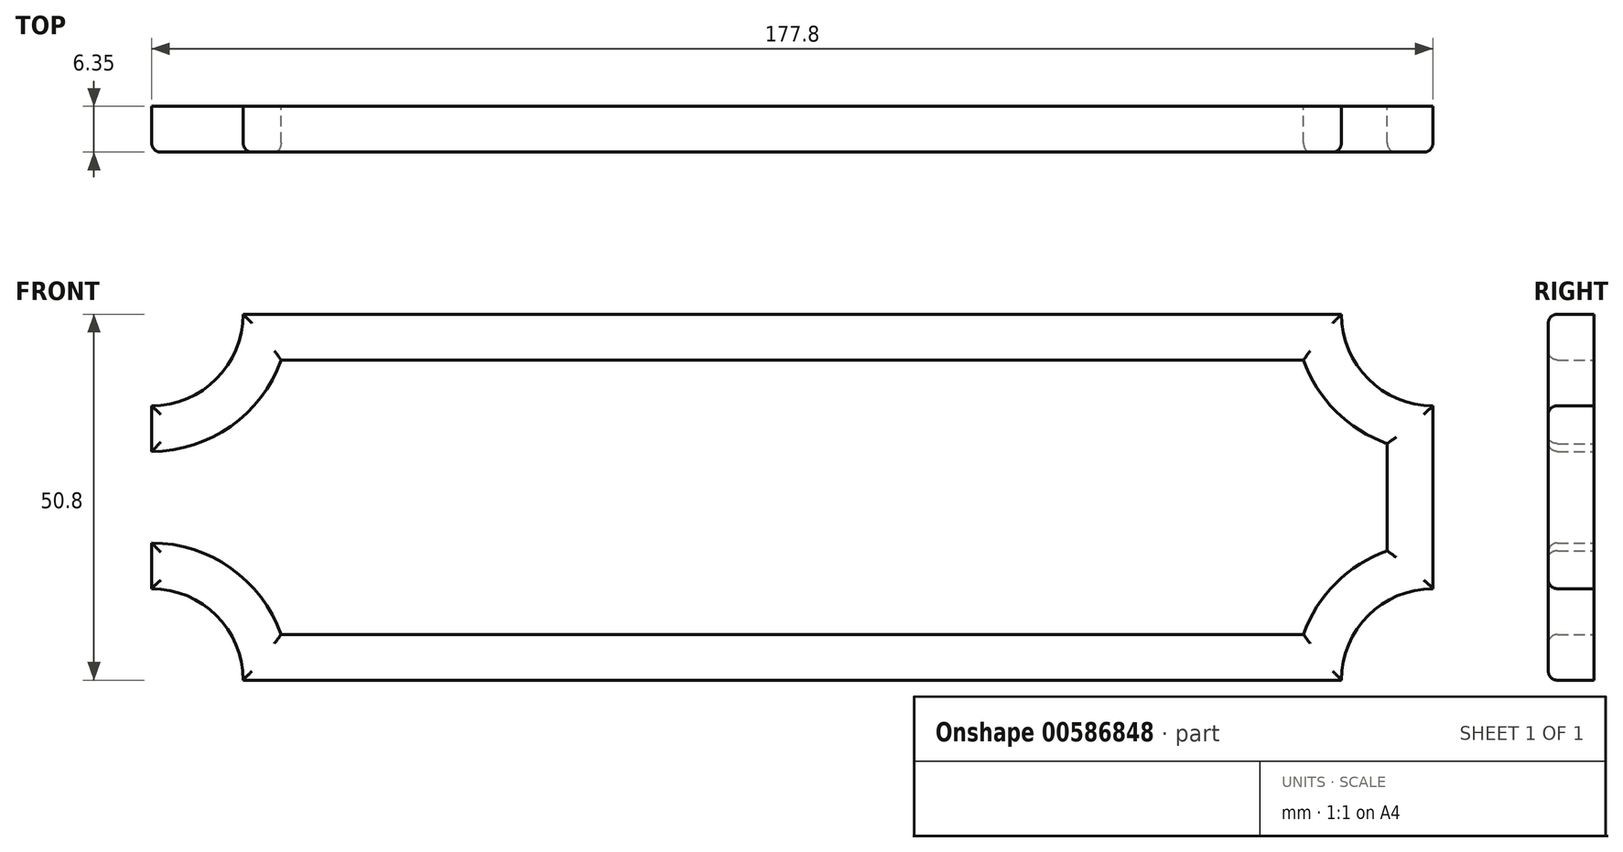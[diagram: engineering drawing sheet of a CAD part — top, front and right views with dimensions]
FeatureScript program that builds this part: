
annotation { "Feature Type Name" : "Feature", "Feature Type Description" : "" }
export const myFeature = defineFeature(function(context is Context, id is Id, definition is map)
    precondition{}
    {
        {
            var Q0;
            Q0=qCreatedBy(makeId("Front.planeOp"),FACE);
            var sketch = newSketch(context, id + "F0", { "sketchPlane" : qUnion([Q0])});
            skLineSegment(sketch, "E0.bottom", {"start": v(-76.2, -25.4) * mm, "end": v(76.2, -25.4) * mm});
            skLineSegment(sketch, "E0.top", {"start": v(-76.2, 25.4) * mm, "end": v(76.2, 25.4) * mm});
            skPoint(sketch, "E0.middle", {"position": v(0, 0) * mm});
            skLineSegment(sketch, "E1.left", {"start": v(-88.9, 12.7) * mm, "end": v(-88.9, -12.7) * mm});
            skLineSegment(sketch, "E1.right", {"start": v(88.9, 12.7) * mm, "end": v(88.9, -12.7) * mm});
            skArc(sketch, "E2", {"start": v(-76.2, -25.4) * mm, "mid": v(-79.92, -16.42) * mm, "end": v(-88.9, -12.7) * mm});
            skArc(sketch, "E3", {"start": v(-88.9, 12.7) * mm, "mid": v(-79.92, 16.42) * mm, "end": v(-76.2, 25.4) * mm});
            skArc(sketch, "E4", {"start": v(76.2, 25.4) * mm, "mid": v(79.92, 16.42) * mm, "end": v(88.9, 12.7) * mm});
            skArc(sketch, "E5", {"start": v(88.9, -12.7) * mm, "mid": v(79.92, -16.42) * mm, "end": v(76.2, -25.4) * mm});
            skArc(sketch, "E6.0", {"start": v(-88.9, 6.35) * mm, "mid": v(-75.43, 11.93) * mm, "end": v(-69.85, 25.4) * mm});
            skArc(sketch, "E7.0", {"start": v(-69.85, -25.4) * mm, "mid": v(-75.43, -11.93) * mm, "end": v(-88.9, -6.35) * mm});
            skArc(sketch, "E8.0", {"start": v(88.9, -6.35) * mm, "mid": v(75.43, -11.93) * mm, "end": v(69.85, -25.4) * mm});
            skArc(sketch, "E9.0", {"start": v(69.85, 25.4) * mm, "mid": v(75.43, 11.93) * mm, "end": v(88.9, 6.35) * mm});
            skLineSegment(sketch, "E10.0", {"start": v(-76.2, 19.05) * mm, "end": v(76.2, 19.05) * mm});
            skLineSegment(sketch, "E11.0", {"start": v(-76.2, -19.05) * mm, "end": v(76.2, -19.05) * mm});
            skLineSegment(sketch, "E12", {"start": v(-88.9, -6.35) * mm, "end": v(-88.9, 6.35) * mm});
            skLineSegment(sketch, "E13.0", {"start": v(-82.55, 12.7) * mm, "end": v(-82.55, -12.7) * mm});
            skLineSegment(sketch, "E14.0", {"start": v(82.55, 12.7) * mm, "end": v(82.55, -12.7) * mm});
            skSolve(sketch);
        }
        {
            var Q0;
            {var subQ0=sQuery(id+"F0.wireOp",EDGE,"E6.0");var subQ1=sQuery(id+"F0.wireOp",EDGE,"E0.top");var subQ2=makeQuery(id+"F0.imprint","INTERSECT",VERTEX,{"derivedFrom":[subQ1,subQ0]});Q0=makeQuery(id+"F0.imprint","IMPRINT",FACE,{"disambiguationData":[TD([[makeQuery(id+"F0.imprint","IMPRINT",EDGE,{"disambiguationData":[TD([[subQ2,-1.0]])],"derivedFrom":subQ1}),-1.0]])]});}
            var Q1;
            {var subQ4=sQuery(id+"F0.wireOp",EDGE,"E3");Q1=makeQuery(id+"F0.imprint","IMPRINT",FACE,{"disambiguationData":[TD([[makeQuery(id+"F0.imprint","IMPRINT",EDGE,{"derivedFrom":subQ4}),-1.0]])]});}
            var Q2;
            {var subQ4=sQuery(id+"F0.wireOp",EDGE,"E2");Q2=makeQuery(id+"F0.imprint","IMPRINT",FACE,{"disambiguationData":[TD([[makeQuery(id+"F0.imprint","IMPRINT",EDGE,{"derivedFrom":subQ4}),-1.0]])]});}
            var Q3;
            {var subQ0=sQuery(id+"F0.wireOp",EDGE,"E12");Q3=makeQuery(id+"F0.imprint","IMPRINT",FACE,{"disambiguationData":[TD([[makeQuery(id+"F0.imprint","IMPRINT",EDGE,{"derivedFrom":subQ0}),-1.0]])]});}
            var Q4;
            {var subQ0=sQuery(id+"F0.wireOp",EDGE,"E7.0");var subQ1=sQuery(id+"F0.wireOp",EDGE,"E0.bottom");var subQ2=makeQuery(id+"F0.imprint","INTERSECT",VERTEX,{"derivedFrom":[subQ1,subQ0]});Q4=makeQuery(id+"F0.imprint","IMPRINT",FACE,{"disambiguationData":[TD([[makeQuery(id+"F0.imprint","IMPRINT",EDGE,{"disambiguationData":[TD([[subQ2,-1.0]])],"derivedFrom":subQ1}),1.0]])]});}
            var Q5;
            {var subQ4=sQuery(id+"F0.wireOp",EDGE,"E5");Q5=makeQuery(id+"F0.imprint","IMPRINT",FACE,{"disambiguationData":[TD([[makeQuery(id+"F0.imprint","IMPRINT",EDGE,{"derivedFrom":subQ4}),-1.0]])]});}
            var Q6;
            {var subQ0=sQuery(id+"F0.wireOp",EDGE,"E8.0");var subQ1=sQuery(id+"F0.wireOp",EDGE,"E1.right");var subQ2=makeQuery(id+"F0.imprint","INTERSECT",VERTEX,{"derivedFrom":[subQ1,subQ0]});Q6=makeQuery(id+"F0.imprint","IMPRINT",FACE,{"disambiguationData":[TD([[makeQuery(id+"F0.imprint","IMPRINT",EDGE,{"disambiguationData":[TD([[subQ2,1.0]])],"derivedFrom":subQ1}),-1.0]])]});}
            var Q7;
            {var subQ4=sQuery(id+"F0.wireOp",EDGE,"E4");Q7=makeQuery(id+"F0.imprint","IMPRINT",FACE,{"disambiguationData":[TD([[makeQuery(id+"F0.imprint","IMPRINT",EDGE,{"derivedFrom":subQ4}),-1.0]])]});}
            extrude(context, id + "F1", {"entities" : qUnion([Q0, Q1, Q2, Q3, Q4, Q5, Q6, Q7]), "depth" : 6.35 * mm, "offsetDistance" : 25.4 * mm});
        }
        {
            var Q0;
            Q0=makeQuery(id+"F1.opExtrude","CAP_EDGE",EDGE,{"disambiguationData":[OSD([sQuery(id+"F0.wireOp",EDGE,"E3")])],"isStart":false});
            var Q1;
            Q1=makeQuery(id+"F1.opExtrude","CAP_EDGE",EDGE,{"disambiguationData":[OSD([sQuery(id+"F0.wireOp",EDGE,"E1.left"),sQuery(id+"F0.wireOp",EDGE,"E12")])],"isStart":false});
            var Q2;
            Q2=makeQuery(id+"F1.opExtrude","CAP_EDGE",EDGE,{"disambiguationData":[OSD([sQuery(id+"F0.wireOp",EDGE,"E2")])],"isStart":false});
            var Q3;
            Q3=makeQuery(id+"F1.opExtrude","CAP_EDGE",EDGE,{"disambiguationData":[OSD([sQuery(id+"F0.wireOp",EDGE,"E0.bottom")])],"isStart":false});
            var Q4;
            Q4=makeQuery(id+"F1.opExtrude","CAP_EDGE",EDGE,{"disambiguationData":[OSD([sQuery(id+"F0.wireOp",EDGE,"E0.top")])],"isStart":false});
            var Q5;
            Q5=makeQuery(id+"F1.opExtrude","CAP_EDGE",EDGE,{"disambiguationData":[OSD([sQuery(id+"F0.wireOp",EDGE,"E4")])],"isStart":false});
            var Q6;
            Q6=makeQuery(id+"F1.opExtrude","CAP_EDGE",EDGE,{"disambiguationData":[OSD([sQuery(id+"F0.wireOp",EDGE,"E1.right")])],"isStart":false});
            var Q7;
            Q7=makeQuery(id+"F1.opExtrude","CAP_EDGE",EDGE,{"disambiguationData":[OSD([sQuery(id+"F0.wireOp",EDGE,"E5")])],"isStart":false});
            var Q8;
            Q8=makeQuery(id+"F1.opExtrude","CAP_EDGE",EDGE,{"disambiguationData":[OSD([sQuery(id+"F0.wireOp",EDGE,"E14.0")])],"isStart":false});
            var Q9;
            Q9=makeQuery(id+"F1.opExtrude","CAP_EDGE",EDGE,{"disambiguationData":[OSD([sQuery(id+"F0.wireOp",EDGE,"E9.0")])],"isStart":false});
            var Q10;
            Q10=makeQuery(id+"F1.opExtrude","CAP_EDGE",EDGE,{"disambiguationData":[OSD([sQuery(id+"F0.wireOp",EDGE,"E10.0")])],"isStart":false});
            var Q11;
            Q11=makeQuery(id+"F1.opExtrude","CAP_EDGE",EDGE,{"disambiguationData":[OSD([sQuery(id+"F0.wireOp",EDGE,"E6.0")])],"isStart":false});
            var Q12;
            Q12=makeQuery(id+"F1.opExtrude","CAP_EDGE",EDGE,{"disambiguationData":[OSD([sQuery(id+"F0.wireOp",EDGE,"E13.0")])],"isStart":false});
            var Q13;
            Q13=makeQuery(id+"F1.opExtrude","CAP_EDGE",EDGE,{"disambiguationData":[OSD([sQuery(id+"F0.wireOp",EDGE,"E7.0")])],"isStart":false});
            var Q14;
            Q14=makeQuery(id+"F1.opExtrude","CAP_EDGE",EDGE,{"disambiguationData":[OSD([sQuery(id+"F0.wireOp",EDGE,"E11.0")])],"isStart":false});
            var Q15;
            Q15=makeQuery(id+"F1.opExtrude","CAP_EDGE",EDGE,{"disambiguationData":[OSD([sQuery(id+"F0.wireOp",EDGE,"E8.0")])],"isStart":false});
            fillet(context, id + "F2", {"entities" : qUnion([Q0, Q1, Q2, Q3, Q4, Q5, Q6, Q7, Q8, Q9, Q10, Q11, Q12, Q13, Q14, Q15]), "radius" : 1.27 * mm, "tangentPropagation" : true, "allowEdgeOverflow" : false});
        }
    });
